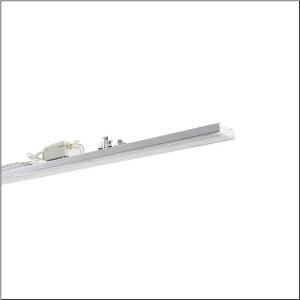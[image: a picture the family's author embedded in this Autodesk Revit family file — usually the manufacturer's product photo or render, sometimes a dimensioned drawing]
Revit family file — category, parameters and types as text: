
# Revit family: licross_r__21_recessed_mo_52tl18cn49xg_ed6d
name_source: partatom
category: Lighting Fixtures
units: mm (PartAtom-declared; Revit-internal decimal feet)

## family parameters
Cut with Voids When Loaded = No
Host = Face
Light Source = No
Part Type = Normal
Room Calculation Point = No
Round Connector Dimension = Use Diameter
Shared = No

## types (1)
- --- (1 x LED, 9000 lm, 49.9 W, 4000K)
    Apparent Load = 50 VA
    CIE Flux Codes = 79 95 99 100 100
    Color Rendering = 80
    Color Temperature = 4000K
    Default Elevation = 1800 mm
    Description = Licross® 21 Recessed MO, luminaire insert, of sheet steel, galvanised, coil coated, white, length: 1.500mm, width: 66mm, height: 67mm, LED rated luminous flux: 9.000lm, light colour: 840, control gear: ON/OFF Multilumen, CLOi, control gear: ECG Multilumen, with plug, 3-pole, with phase selection, mains connection: 220..240V, AC, 50/60Hz, halogen-free wiring, primary light control with lens, of plastic, primary optical cover: cover, of PMMA, light emission: direct distribution, primary light characteristic: symmetric, protection rating (complete): IP40, insulation class (complete): insulation class I (protective earthing), certification: CE, ENEC, VDE, UKCA, protection symbol: D if used in an environment without relevant dust loads with corresponding accessories, impact resistance: IK06, permissible ambient temperature for indoor applications: -35..+40°C, corresponds to IFS (International Featured Standards) requirements for safety and quality in the food industry, reducing of maximum allowable ambient temperature of 5°C with ceiling mounting, LABS conformity tested according to VDMA 24364:2018-05, packaging unit: 1 piece
    Height = 58 mm
    Lamp = 1 x LED
    Lamp Light Flux = 9000 lm
    Lamp Power = 49.9 W
    Lamp count = 1
    Length = 1500 mm
    Luminous efficacy = 180 lm/W
    Manufacturer = Siteco
    ModVariant = No
    Model = 52TL18CN49XG
    Mounting Place = Ceiling
    Mounting Type = Pendant
    Number of Poles = 1
    OnlyDefault = Yes
    Power Factor = 1
    Product Name = Licross® 21 Recessed MO
    Product group = luminaire insert
    ProductGroupID = 901
    Protection Class = Protection class I
    Protection Degree = IP 40
    RLX_Detail_Level = 1
    RLX_Emergency_Light_Flux = 0 lm
    RLX_Emergency_Type = 0
    RLX_Emergency_Type_DB = No
    RlxData = <blob elided: 22285 chars, md5=f74d6835>
    Socket = socket
    Standby Power = 0 W
    System Light Flux = 9000 lm
    System Power = 50 W
    Type Comments = factory setting: luminous flux: 100 % | (A | C | E) | 116 mA
    Type Image = l_1296930.jpg
    URL = http://relux.com
    VarID = @adj_040161
    Voltage = 0 V
    Weight = 0.00 kg
    Width = 66 mm

## geometry (parser evidence)
native form markers: Blend x4, Sweep x12
no freeform markers — native parametric forms only
